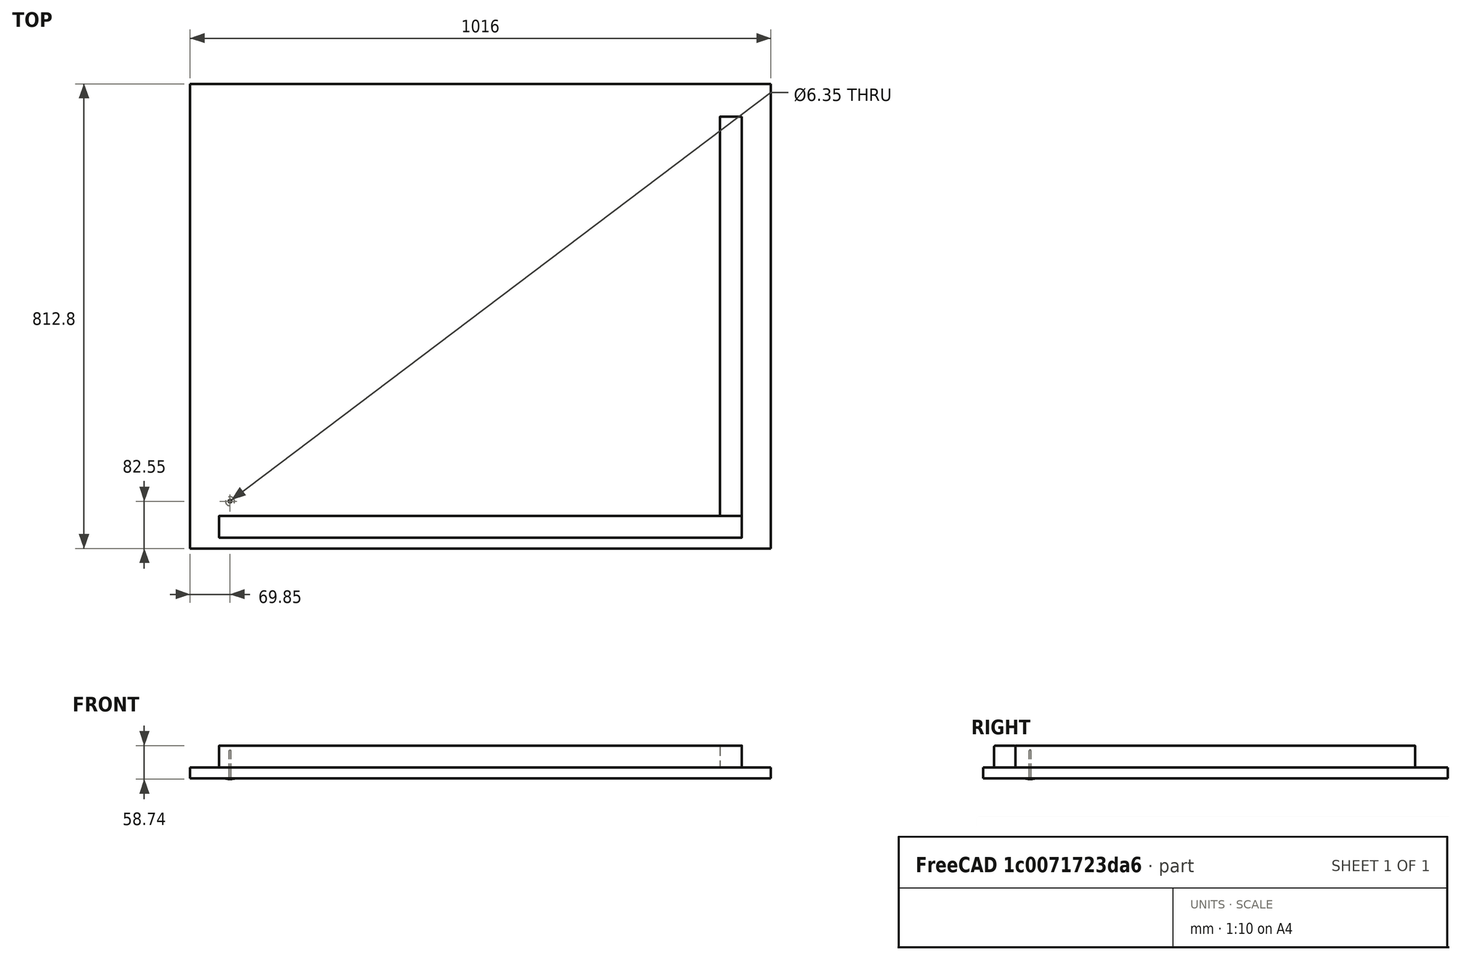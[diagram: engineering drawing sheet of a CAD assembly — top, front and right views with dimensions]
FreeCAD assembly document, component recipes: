
FREECAD ASSEMBLY — COMPONENT RECIPES ("Lid")

This assembly document has 15 components, labeled P0..P14 below (a component is one placed body or linked part). 0 of them carry a construction recipe — the FreeCAD feature program that regenerates the part from scratch, quoted from this document or its linked companion documents; the rest are supplied as boundary geometry only. No exploded tour is included for this assembly.
COMPONENT P0 — geometry summary ("LF_A001"; no construction recipe available for this part):
  bounding box: 914.4 x 38.1 x 38.1 mm
  tessellated surface: 220 triangles
  volume: 1319440 mm^3 (99% of its bounding box)
  symmetry: 4-fold rotationally symmetric about the x axis; 2-fold rotationally symmetric about the y axis; 2-fold rotationally symmetric about the z axis; mirror-symmetric across its x mid-plane, y mid-plane, z mid-plane
COMPONENT P1 — geometry summary ("LF_B001"; no construction recipe available for this part):
  bounding box: 698.5 x 38.1 x 38.1 mm
  tessellated surface: 220 triangles
  volume: 1007905 mm^3 (99% of its bounding box)
  symmetry: 2-fold rotationally symmetric about the x axis; 4-fold rotationally symmetric about the y axis; 2-fold rotationally symmetric about the z axis; mirror-symmetric across its x mid-plane, z mid-plane
COMPONENT P2 — geometry summary ("Screw_w_Washer_B006"; no construction recipe available for this part):
  bounding box: 50.8 x 15.9 x 15.9 mm
  tessellated surface: 2,456 triangles
  volume: 650 mm^3 (5% of its bounding box)
  symmetry: 4-fold rotationally symmetric about the z axis; mirror-symmetric across its x mid-plane
COMPONENT P3 — geometry summary ("Screw_w_Washer_B007"; no construction recipe available for this part):
  bounding box: 50.8 x 15.9 x 15.9 mm
  tessellated surface: 2,456 triangles
  volume: 650 mm^3 (5% of its bounding box)
  symmetry: 4-fold rotationally symmetric about the z axis; mirror-symmetric across its y mid-plane
COMPONENT P4 — geometry summary ("Screw_w_Washer_B008"; no construction recipe available for this part):
  bounding box: 50.8 x 15.9 x 15.9 mm
  tessellated surface: 2,456 triangles
  volume: 650 mm^3 (5% of its bounding box)
  symmetry: 4-fold rotationally symmetric about the z axis; mirror-symmetric across its x mid-plane
COMPONENT P5 — geometry summary ("Screw_w_Washer_B009"; no construction recipe available for this part):
  bounding box: 50.8 x 15.9 x 15.9 mm
  tessellated surface: 2,456 triangles
  volume: 650 mm^3 (5% of its bounding box)
  symmetry: 4-fold rotationally symmetric about the z axis; mirror-symmetric across its x mid-plane
COMPONENT P6 — geometry summary ("Screw_w_Washer_B010"; no construction recipe available for this part):
  bounding box: 50.8 x 15.9 x 15.9 mm
  tessellated surface: 2,456 triangles
  volume: 650 mm^3 (5% of its bounding box)
  symmetry: 4-fold rotationally symmetric about the z axis; mirror-symmetric across its x mid-plane
COMPONENT P7 — geometry summary ("Screw_w_Washer_B011"; no construction recipe available for this part):
  bounding box: 50.8 x 15.9 x 15.9 mm
  tessellated surface: 2,456 triangles
  volume: 650 mm^3 (5% of its bounding box)
  symmetry: 4-fold rotationally symmetric about the z axis; mirror-symmetric across its x mid-plane
COMPONENT P8 — geometry summary ("Screw_w_Washer_B019"; no construction recipe available for this part):
  bounding box: 50.8 x 15.9 x 15.9 mm
  tessellated surface: 2,456 triangles
  volume: 650 mm^3 (5% of its bounding box)
  symmetry: 4-fold rotationally symmetric about the z axis; mirror-symmetric across its x mid-plane
COMPONENT P9 — geometry summary ("Screw_w_Washer_B020"; no construction recipe available for this part):
  bounding box: 50.8 x 15.9 x 15.9 mm
  tessellated surface: 2,456 triangles
  volume: 650 mm^3 (5% of its bounding box)
  symmetry: 4-fold rotationally symmetric about the z axis; mirror-symmetric across its x mid-plane
COMPONENT P10 — geometry summary ("Screw_w_Washer_B021"; no construction recipe available for this part):
  bounding box: 50.8 x 15.9 x 15.9 mm
  tessellated surface: 2,456 triangles
  volume: 650 mm^3 (5% of its bounding box)
  symmetry: 4-fold rotationally symmetric about the z axis; mirror-symmetric across its x mid-plane
COMPONENT P11 — geometry summary ("Screw_w_Washer_B022"; no construction recipe available for this part):
  bounding box: 50.8 x 15.9 x 15.9 mm
  tessellated surface: 2,456 triangles
  volume: 650 mm^3 (5% of its bounding box)
  symmetry: 4-fold rotationally symmetric about the z axis; mirror-symmetric across its x mid-plane
COMPONENT P12 — geometry summary ("Screw_w_Washer_B023"; no construction recipe available for this part):
  bounding box: 50.8 x 15.9 x 15.9 mm
  tessellated surface: 2,456 triangles
  volume: 650 mm^3 (5% of its bounding box)
  symmetry: 4-fold rotationally symmetric about the z axis; mirror-symmetric across its x mid-plane
COMPONENT P13 — geometry summary ("Screw_w_Washer_B024"; no construction recipe available for this part):
  bounding box: 50.8 x 15.9 x 15.9 mm
  tessellated surface: 2,456 triangles
  volume: 650 mm^3 (5% of its bounding box)
  symmetry: 4-fold rotationally symmetric about the z axis; mirror-symmetric across its x mid-plane
COMPONENT P14 — geometry summary ("Screw_w_Washer_B025"; no construction recipe available for this part):
  bounding box: 50.8 x 15.9 x 15.9 mm
  tessellated surface: 2,456 triangles
  volume: 650 mm^3 (5% of its bounding box)
  symmetry: 4-fold rotationally symmetric about the z axis; mirror-symmetric across its x mid-plane
PROVENANCE & LICENSES
A FreeCAD (.FCStd) document from a public repository crawl; recipes are the document's own serialized feature recipes (and, for linked parts, companion documents' recipes).
License: gpl-3.0.
